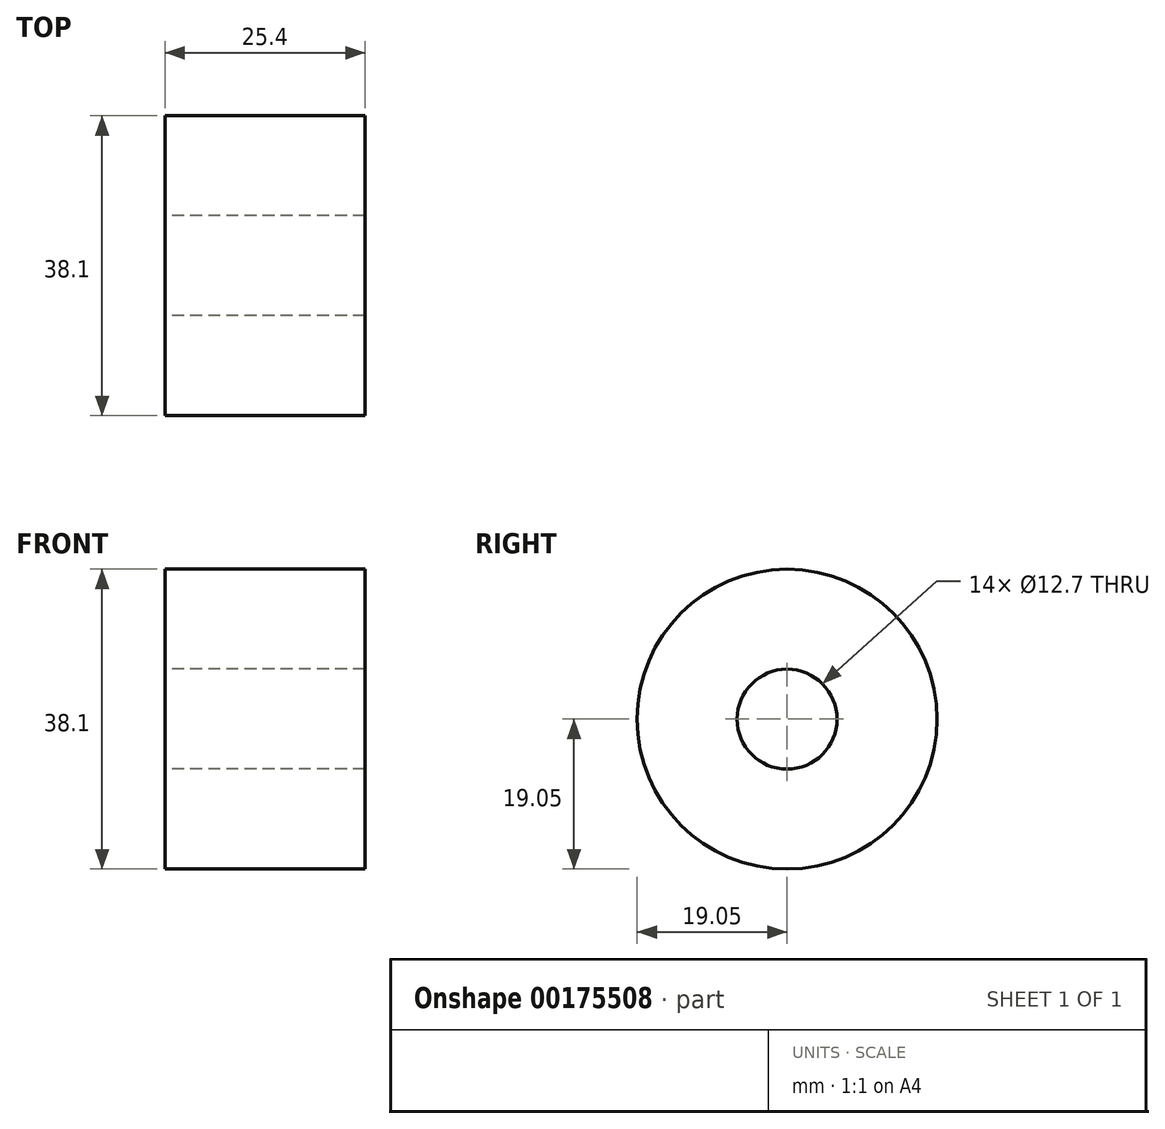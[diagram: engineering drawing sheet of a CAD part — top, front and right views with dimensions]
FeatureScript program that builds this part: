
annotation { "Feature Type Name" : "Feature", "Feature Type Description" : "" }
export const myFeature = defineFeature(function(context is Context, id is Id, definition is map)
    precondition{}
    {
        {
            var Q0;
            Q0=qCreatedBy(makeId("Right.planeOp"),FACE);
            var sketch = newSketch(context, id + "F0", { "sketchPlane" : qUnion([Q0])});
            skCircle(sketch, "E0", {"center": v(0, 0) * mm, "radius": 19.05 * mm});
            skCircle(sketch, "E1", {"center": v(0, 0) * mm, "radius": 6.35 * mm});
            skSolve(sketch);
        }
        {
            var Q0;
            Q0=makeQuery(id+"F0.imprint","IMPRINT",FACE,{"disambiguationData":[TD([[makeQuery(id+"F0.imprint","IMPRINT",EDGE,{"derivedFrom":sQuery(id+"F0.wireOp",EDGE,"E0")}),1.0]])]});
            extrude(context, id + "F1", {"entities" : qUnion([Q0]), "depth" : 25.4 * mm});
        }
    });
